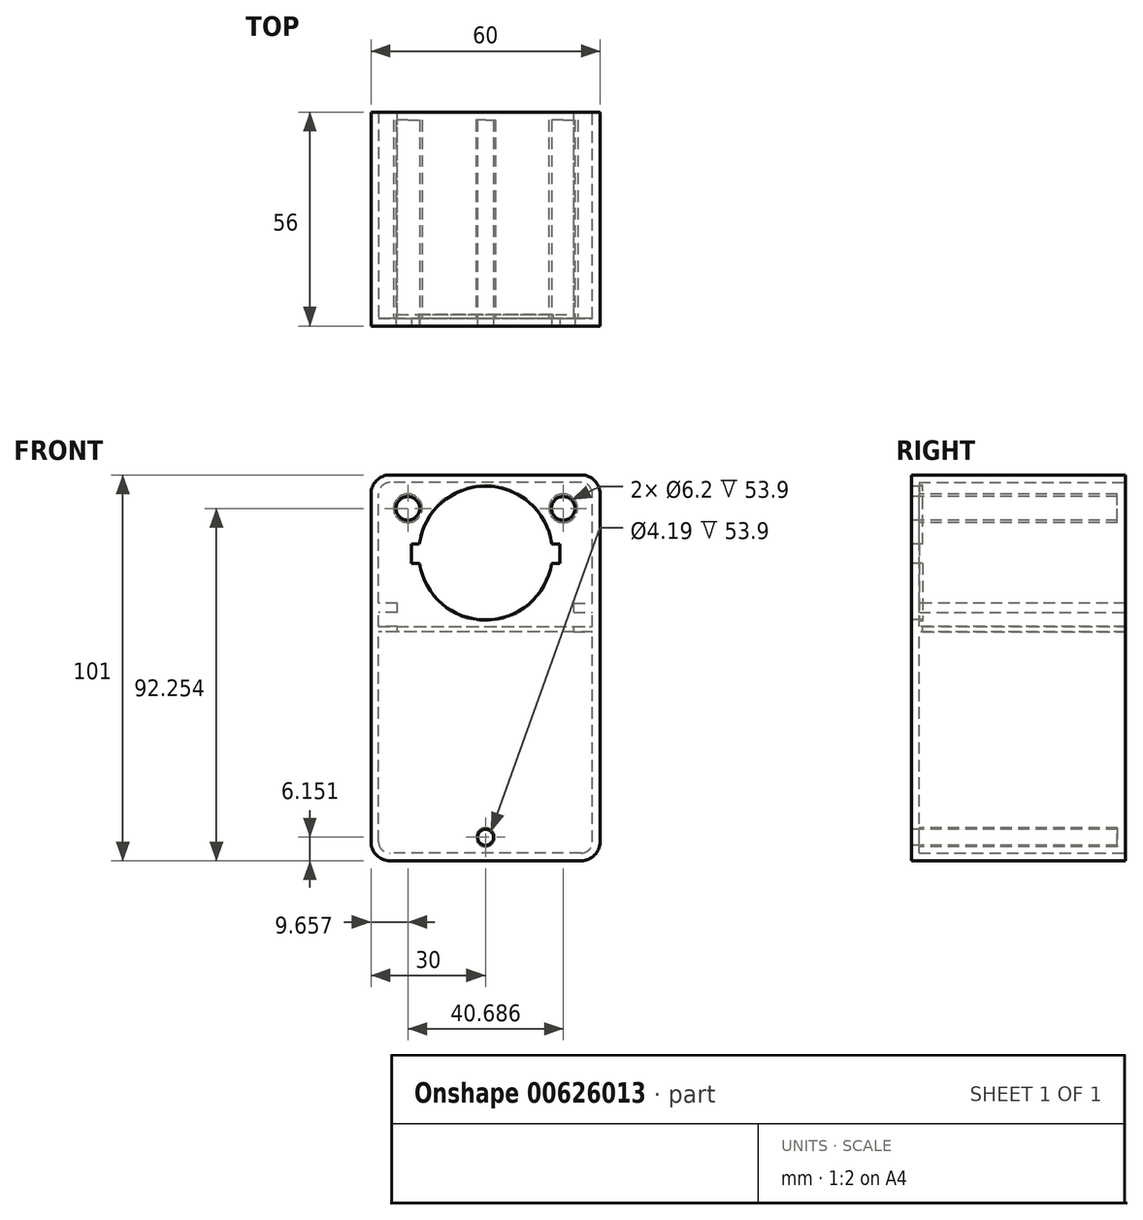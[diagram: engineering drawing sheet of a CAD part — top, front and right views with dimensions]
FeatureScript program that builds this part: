
annotation { "Feature Type Name" : "Feature", "Feature Type Description" : "" }
export const myFeature = defineFeature(function(context is Context, id is Id, definition is map)
    precondition{}
    {
        {
            var Q0;
            Q0=qCreatedBy(makeId("Front.planeOp"),FACE);
            var sketch = newSketch(context, id + "F0", { "sketchPlane" : qUnion([Q0])});
            skLineSegment(sketch, "E0.bottom", {"start": v(30, -50.5) * mm, "end": v(-30, -50.5) * mm});
            skLineSegment(sketch, "E0.top", {"start": v(30, 50.5) * mm, "end": v(-30, 50.5) * mm});
            skLineSegment(sketch, "E0.left", {"start": v(30, -50.5) * mm, "end": v(30, 50.5) * mm});
            skLineSegment(sketch, "E0.right", {"start": v(-30, -50.5) * mm, "end": v(-30, 50.5) * mm});
            skPoint(sketch, "E0.middle", {"position": v(0, 0) * mm});
            skSolve(sketch);
        }
        {
            var Q0;
            Q0 = qSketchRegion(id + "F0", true);
            extrude(context, id + "F1", {"entities" : qUnion([Q0]), "depth" : 56 * mm, "offsetDistance" : 25 * mm, "symmetric" : true});
        }
        {
            var Q0;
            Q0=makeQuery(id+"F1.opExtrude","SWEPT_EDGE",EDGE,{"disambiguationData":[OSD([sQuery(id+"F0.wireOp",EDGE,"E0.top"),sQuery(id+"F0.wireOp",EDGE,"E0.right")])]});
            var Q1;
            Q1=makeQuery(id+"F1.opExtrude","SWEPT_EDGE",EDGE,{"disambiguationData":[OSD([sQuery(id+"F0.wireOp",EDGE,"E0.top"),sQuery(id+"F0.wireOp",EDGE,"E0.left")])]});
            var Q2;
            Q2=makeQuery(id+"F1.opExtrude","SWEPT_EDGE",EDGE,{"disambiguationData":[OSD([sQuery(id+"F0.wireOp",EDGE,"E0.bottom"),sQuery(id+"F0.wireOp",EDGE,"E0.left")])]});
            var Q3;
            Q3=makeQuery(id+"F1.opExtrude","SWEPT_EDGE",EDGE,{"disambiguationData":[OSD([sQuery(id+"F0.wireOp",EDGE,"E0.bottom"),sQuery(id+"F0.wireOp",EDGE,"E0.right")])]});
            fillet(context, id + "F2", {"entities" : qUnion([Q0, Q1, Q2, Q3]), "radius" : 5 * mm, "tangentPropagation" : true, "allowEdgeOverflow" : false});
        }
        {
            var Q0;
            Q0=makeQuery(id+"F1.opExtrude","CAP_FACE",FACE,{"disambiguationData":[OSD([sQuery(id+"F0.wireOp",EDGE,"E0.bottom"),sQuery(id+"F0.wireOp",EDGE,"E0.top"),sQuery(id+"F0.wireOp",EDGE,"E0.left"),sQuery(id+"F0.wireOp",EDGE,"E0.right")])],"isStart":true});
            shell(context, id + "F3", {"entities" : qUnion([Q0]), "thickness" : 2 * mm});
        }
        {
            var Q0;
            Q0=makeQuery(id+"F1.opExtrude","CAP_FACE",FACE,{"disambiguationData":[OSD([sQuery(id+"F0.wireOp",EDGE,"E0.bottom"),sQuery(id+"F0.wireOp",EDGE,"E0.top"),sQuery(id+"F0.wireOp",EDGE,"E0.left"),sQuery(id+"F0.wireOp",EDGE,"E0.right")])],"isStart":false});
            var sketch = newSketch(context, id + "F4", { "sketchPlane" : qUnion([Q0])});
            skCircle(sketch, "E1", {"center": v(0, 30.06) * mm, "radius": 17.5 * mm});
            skSolve(sketch);
        }
        {
            var Q0;
            Q0 = qSketchRegion(id + "F4", true);
            extrude(context, id + "F5", {"entities" : qUnion([Q0]), "operationType" : NewBodyOperationType.REMOVE, "oppositeDirection" : true, "depth" : 104.5 * mm, "offsetDistance" : 25 * mm});
        }
        {
            var Q0;
            Q0=makeQuery(id+"F3.opShell","OFFSET_FACE",FACE,{"disambiguationData":[OSD([sQuery(id+"F0.wireOp",EDGE,"E0.bottom"),sQuery(id+"F0.wireOp",EDGE,"E0.top"),sQuery(id+"F0.wireOp",EDGE,"E0.left"),sQuery(id+"F0.wireOp",EDGE,"E0.right")])]});
            var sketch = newSketch(context, id + "F6", { "sketchPlane" : qUnion([Q0])});
            skLineSegment(sketch, "E2", {"start": v(0, 10.82) * mm, "end": v(-28, 10.82) * mm});
            skLineSegment(sketch, "E3", {"start": v(-28, 10.82) * mm, "end": v(-28, 9.47) * mm});
            skLineSegment(sketch, "E4", {"start": v(-28, 9.47) * mm, "end": v(0, 9.47) * mm});
            skLineSegment(sketch, "E5", {"start": v(0, 9.47) * mm, "end": v(0, 10.82) * mm});
            skPoint(sketch, "E6.startSnap0", {"position": v(28, 0) * mm});
            skArc(sketch, "E7", {"start": v(0, 12.27) * mm, "mid": v(-17.8, 30.06) * mm, "end": v(0, 47.85) * mm});
            skLineSegment(sketch, "E8", {"start": v(0, 47.85) * mm, "end": v(0, 47.56) * mm});
            skLineSegment(sketch, "E9", {"start": v(0, 12.56) * mm, "end": v(0, 12.27) * mm});
            skArc(sketch, "E10", {"start": v(0, 12.56) * mm, "mid": v(-17.5, 30.06) * mm, "end": v(0, 47.56) * mm});
            skSolve(sketch);
        }
        {
            var Q0;
            Q0 = qSketchRegion(id + "F6", true);
            extrude(context, id + "F7", {"entities" : qUnion([Q0]), "operationType" : NewBodyOperationType.ADD, "depth" : 1 * mm, "offsetDistance" : 25 * mm});
        }
        {
            var Q0;
            Q0=makeQuery(id+"F3.opShell","OFFSET_FACE",FACE,{"disambiguationData":[OSD([sQuery(id+"F0.wireOp",EDGE,"E0.left")])]});
            var sketch = newSketch(context, id + "F8", { "sketchPlane" : qUnion([Q0])});
            skLineSegment(sketch, "E11", {"start": v(26, 10.82) * mm, "end": v(-28, 10.82) * mm});
            skLineSegment(sketch, "E12", {"start": v(-28, 10.82) * mm, "end": v(25, 10.82) * mm});
            skLineSegment(sketch, "E13", {"start": v(25, 10.82) * mm, "end": v(25, 9.47) * mm});
            skLineSegment(sketch, "E14", {"start": v(25, 9.47) * mm, "end": v(-28, 9.47) * mm});
            skLineSegment(sketch, "E15", {"start": v(-28, 9.47) * mm, "end": v(-28, 10.82) * mm});
            skLineSegment(sketch, "E16", {"start": v(26, 14.48) * mm, "end": v(-28, 14.48) * mm});
            skLineSegment(sketch, "E17", {"start": v(-28, 14.48) * mm, "end": v(-28, 16.9) * mm});
            skLineSegment(sketch, "E18", {"start": v(-28, 16.9) * mm, "end": v(26, 16.9) * mm});
            skLineSegment(sketch, "E19", {"start": v(26, 16.9) * mm, "end": v(26, 14.48) * mm});
            skSolve(sketch);
        }
        {
            var Q0;
            Q0 = qSketchRegion(id + "F8", true);
            extrude(context, id + "F9", {"entities" : qUnion([Q0]), "operationType" : NewBodyOperationType.ADD, "depth" : 4.9 * mm, "offsetDistance" : 25 * mm});
        }
        {
            var Q0;
            Q0=makeQuery(id+"F1.opExtrude","SWEPT_BODY",BODY,{"disambiguationData":[OSD([sQuery(id+"F0.wireOp",EDGE,"E0.bottom"),sQuery(id+"F0.wireOp",EDGE,"E0.top"),sQuery(id+"F0.wireOp",EDGE,"E0.left"),sQuery(id+"F0.wireOp",EDGE,"E0.right")])]});
            var Q1;
            Q1=qCreatedBy(makeId("Right.planeOp"),FACE);
            mirror(context, id + "F10", {"operationType" : NewBodyOperationType.ADD, "entities" : qUnion([Q0]), "mirrorPlane" : qUnion([Q1])});
        }
        {
            var Q0;
            {var subQ1=sQuery(id+"F0.wireOp",EDGE,"E0.left");var subQ6=sQuery(id+"F0.wireOp",EDGE,"E0.right");var subQ7=sQuery(id+"F0.wireOp",EDGE,"E0.top");Q0=makeQuery(id+"F10.boolean.opBoolean","SPLIT",FACE,{"disambiguationData":[TD([makeQuery(id+"F3.opShell","OFFSET_FACE",FACE,{"disambiguationData":[OSD([subQ7])]})])],"derivedFrom":makeQuery(id+"F3.opShell","OFFSET_FACE",FACE,{"disambiguationData":[OSD([sQuery(id+"F0.wireOp",EDGE,"E0.bottom"),subQ7,subQ1,subQ6])]})});}
            var sketch = newSketch(context, id + "F11", { "sketchPlane" : qUnion([Q0])});
            skCircle(sketch, "E20", {"center": v(20.34, 41.75) * mm, "radius": 3.75 * mm});
            skCircle(sketch, "E21", {"center": v(20.34, 41.75) * mm, "radius": 3.1 * mm});
            skArc(sketch, "E22", {"start": v(0, -46.85) * mm, "mid": v(2.5, -44.35) * mm, "end": v(0, -41.85) * mm});
            skArc(sketch, "E23.0", {"start": v(0, -46.44) * mm, "mid": v(2.1, -44.35) * mm, "end": v(0, -42.26) * mm});
            skLineSegment(sketch, "E24", {"start": v(0, -46.85) * mm, "end": v(0, -46.44) * mm});
            skLineSegment(sketch, "E25", {"start": v(0, -42.26) * mm, "end": v(0, -41.85) * mm});
            skSolve(sketch);
        }
        {
            var Q0;
            Q0 = qSketchRegion(id + "F11", true);
            extrude(context, id + "F12", {"entities" : qUnion([Q0]), "depth" : 51.9 * mm, "offsetDistance" : 25 * mm});
        }
        {
            var Q0;
            Q0=makeQuery(id+"F12.opExtrude","SWEPT_BODY",BODY,{"disambiguationData":[OSD([sQuery(id+"F11.wireOp",EDGE,"E20"),sQuery(id+"F11.wireOp",EDGE,"E21")])]});
            var Q1;
            Q1=makeQuery(id+"F12.opExtrude","SWEPT_BODY",BODY,{"disambiguationData":[OSD([sQuery(id+"F11.wireOp",EDGE,"E22"),sQuery(id+"F11.wireOp",EDGE,"E23.0"),sQuery(id+"F11.wireOp",EDGE,"E24"),sQuery(id+"F11.wireOp",EDGE,"E25")])]});
            var Q2;
            Q2=qCreatedBy(makeId("Right.planeOp"),FACE);
            mirror(context, id + "F13", {"operationType" : NewBodyOperationType.ADD, "entities" : qUnion([Q0, Q1]), "mirrorPlane" : qUnion([Q2])});
        }
        {
            var Q0;
            {var subQ1=sQuery(id+"F0.wireOp",EDGE,"E0.left");var subQ6=sQuery(id+"F0.wireOp",EDGE,"E0.right");var subQ7=sQuery(id+"F0.wireOp",EDGE,"E0.top");Q0=makeQuery(id+"F13.boolean.opBoolean","SPLIT",FACE,{"disambiguationData":[TD([makeQuery(id+"F13.opPattern","COPY",FACE,{"derivedFrom":makeQuery(id+"F12.opExtrude","SWEPT_FACE",FACE,{"disambiguationData":[OSD([sQuery(id+"F11.wireOp",EDGE,"E21")])]}),"instanceName":"1"})])],"derivedFrom":makeQuery(id+"F10.boolean.opBoolean","SPLIT",FACE,{"disambiguationData":[TD([makeQuery(id+"F3.opShell","OFFSET_FACE",FACE,{"disambiguationData":[OSD([subQ7])]})])],"derivedFrom":makeQuery(id+"F3.opShell","OFFSET_FACE",FACE,{"disambiguationData":[OSD([sQuery(id+"F0.wireOp",EDGE,"E0.bottom"),subQ7,subQ1,subQ6])]})})});}
            var Q1;
            {var subQ1=sQuery(id+"F0.wireOp",EDGE,"E0.left");var subQ6=sQuery(id+"F0.wireOp",EDGE,"E0.right");var subQ7=sQuery(id+"F0.wireOp",EDGE,"E0.top");Q1=makeQuery(id+"F13.boolean.opBoolean","SPLIT",FACE,{"disambiguationData":[TD([makeQuery(id+"F12.opExtrude","SWEPT_FACE",FACE,{"disambiguationData":[OSD([sQuery(id+"F11.wireOp",EDGE,"E21")])]})])],"derivedFrom":makeQuery(id+"F10.boolean.opBoolean","SPLIT",FACE,{"disambiguationData":[TD([makeQuery(id+"F3.opShell","OFFSET_FACE",FACE,{"disambiguationData":[OSD([subQ7])]})])],"derivedFrom":makeQuery(id+"F3.opShell","OFFSET_FACE",FACE,{"disambiguationData":[OSD([sQuery(id+"F0.wireOp",EDGE,"E0.bottom"),subQ7,subQ1,subQ6])]})})});}
            var Q2;
            {var subQ0=makeQuery(id+"F12.opExtrude","SWEPT_FACE",FACE,{"disambiguationData":[OSD([sQuery(id+"F11.wireOp",EDGE,"E23.0")])]});var subQ1=sQuery(id+"F0.wireOp",EDGE,"E0.left");var subQ2=sQuery(id+"F0.wireOp",EDGE,"E0.bottom");var subQ4=sQuery(id+"F0.wireOp",EDGE,"E0.right");Q2=makeQuery(id+"F13.boolean.opBoolean","SPLIT",FACE,{"disambiguationData":[TD([subQ0])],"derivedFrom":makeQuery(id+"F10.boolean.opBoolean","SPLIT",FACE,{"disambiguationData":[TD([makeQuery(id+"F3.opShell","OFFSET_FACE",FACE,{"disambiguationData":[OSD([subQ2])]})])],"derivedFrom":makeQuery(id+"F3.opShell","OFFSET_FACE",FACE,{"disambiguationData":[OSD([subQ2,sQuery(id+"F0.wireOp",EDGE,"E0.top"),subQ1,subQ4])]})})});}
            extrude(context, id + "F14", {"entities" : qUnion([Q0, Q1, Q2]), "operationType" : NewBodyOperationType.REMOVE, "oppositeDirection" : true, "depth" : 25 * mm, "offsetDistance" : 25 * mm});
        }
        {
            var Q0;
            Q0=makeQuery(id+"F1.opExtrude","CAP_FACE",FACE,{"disambiguationData":[OSD([sQuery(id+"F0.wireOp",EDGE,"E0.bottom"),sQuery(id+"F0.wireOp",EDGE,"E0.top"),sQuery(id+"F0.wireOp",EDGE,"E0.left"),sQuery(id+"F0.wireOp",EDGE,"E0.right")])],"isStart":false});
            var sketch = newSketch(context, id + "F15", { "sketchPlane" : qUnion([Q0])});
            skLineSegment(sketch, "E26.bottom", {"start": v(-19.4, 32.4) * mm, "end": v(-15.6, 32.4) * mm});
            skLineSegment(sketch, "E26.top", {"start": v(-19.4, 27.4) * mm, "end": v(-15.6, 27.4) * mm});
            skLineSegment(sketch, "E26.left", {"start": v(-19.4, 32.4) * mm, "end": v(-19.4, 27.4) * mm});
            skLineSegment(sketch, "E26.right", {"start": v(-15.6, 32.4) * mm, "end": v(-15.6, 27.4) * mm});
            skPoint(sketch, "E26.middle", {"position": v(-17.5, 29.9) * mm});
            skLineSegment(sketch, "E27.MirrorCS", {"start": v(-19.08, 27.4) * mm, "end": v(-15.5, 27.4) * mm});
            skLineSegment(sketch, "E28.bottom", {"start": v(19.4, 32.4) * mm, "end": v(15.6, 32.4) * mm});
            skLineSegment(sketch, "E28.top", {"start": v(19.4, 27.4) * mm, "end": v(15.6, 27.4) * mm});
            skLineSegment(sketch, "E28.left", {"start": v(19.4, 32.4) * mm, "end": v(19.4, 27.4) * mm});
            skLineSegment(sketch, "E28.right", {"start": v(15.6, 32.4) * mm, "end": v(15.6, 27.4) * mm});
            skPoint(sketch, "E28.middle", {"position": v(17.5, 29.9) * mm});
            skPoint(sketch, "E28.middle.positionSnap0", {"position": v(-15.6, 29.9) * mm});
            skPoint(sketch, "E28.centerSnap0", {"position": v(-15.6, 29.9) * mm});
            skSolve(sketch);
        }
        {
            var Q0;
            {var subQ0=sQuery(id+"F15.wireOp",EDGE,"E26.left");Q0=makeQuery(id+"F15.imprint","IMPRINT",FACE,{"disambiguationData":[TD([[makeQuery(id+"F15.imprint","IMPRINT",EDGE,{"derivedFrom":subQ0}),1.0]])]});}
            var Q1;
            {var subQ0=sQuery(id+"F15.wireOp",EDGE,"E28.left");Q1=makeQuery(id+"F15.imprint","IMPRINT",FACE,{"disambiguationData":[TD([[makeQuery(id+"F15.imprint","IMPRINT",EDGE,{"derivedFrom":subQ0}),-1.0]])]});}
            extrude(context, id + "F16", {"entities" : qUnion([Q0, Q1]), "operationType" : NewBodyOperationType.REMOVE, "oppositeDirection" : true, "depth" : 25 * mm, "offsetDistance" : 25 * mm});
        }
    });
